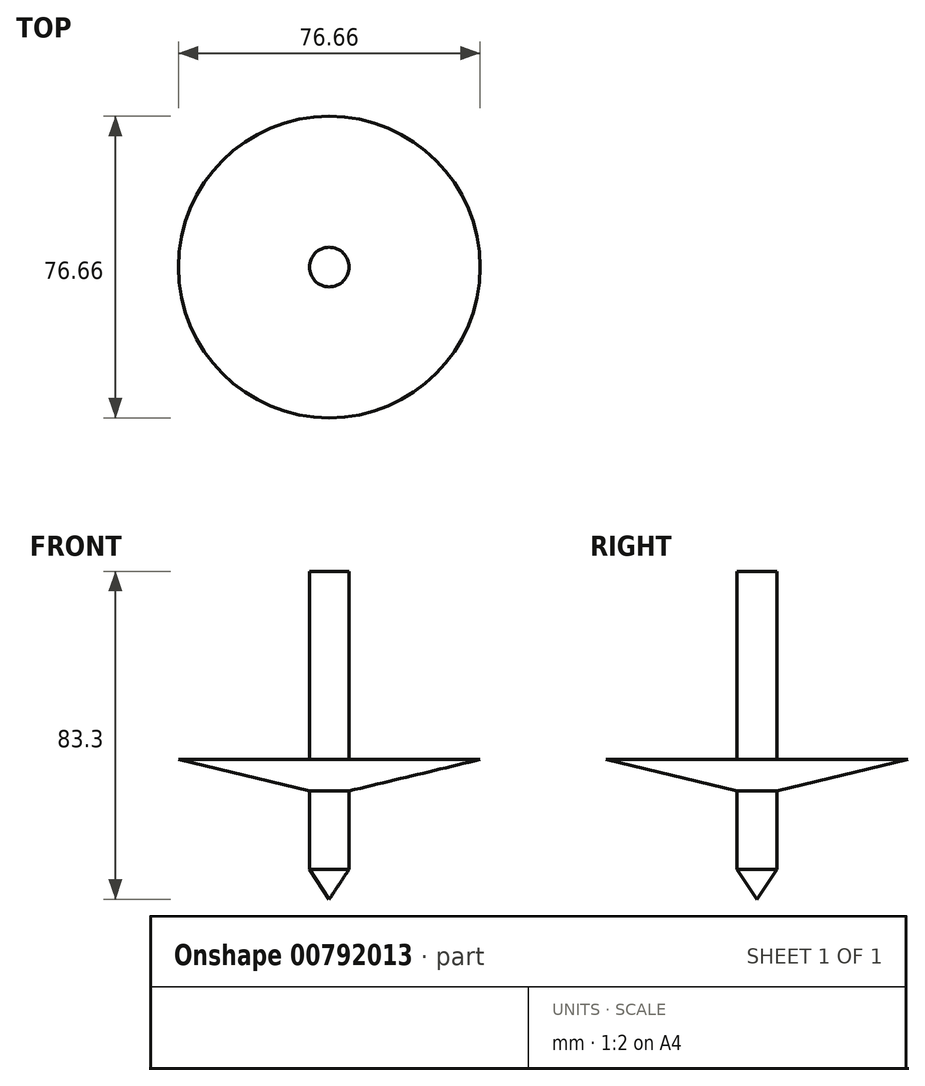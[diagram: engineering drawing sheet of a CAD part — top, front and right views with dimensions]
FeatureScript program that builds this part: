
annotation { "Feature Type Name" : "Feature", "Feature Type Description" : "" }
export const myFeature = defineFeature(function(context is Context, id is Id, definition is map)
    precondition{}
    {
        {
            var Q0;
            Q0=qCreatedBy(makeId("Front.planeOp"),FACE);
            var sketch = newSketch(context, id + "F0", { "sketchPlane" : qUnion([Q0])});
            skLineSegment(sketch, "E0", {"start": v(0, 47.79) * mm, "end": v(5.03, 47.79) * mm});
            skLineSegment(sketch, "E1", {"start": v(5.03, 47.79) * mm, "end": v(5.03, 0) * mm});
            skLineSegment(sketch, "E2", {"start": v(5.03, 0) * mm, "end": v(38.33, 0) * mm});
            skLineSegment(sketch, "E3", {"start": v(38.33, 0) * mm, "end": v(5.03, -7.98) * mm});
            skLineSegment(sketch, "E4", {"start": v(5.03, -7.98) * mm, "end": v(5.03, -27.89) * mm});
            skLineSegment(sketch, "E5", {"start": v(5.03, -27.89) * mm, "end": v(0, -35.5) * mm});
            skLineSegment(sketch, "E6", {"start": v(0, -35.5) * mm, "end": v(0, 47.79) * mm});
            skLineSegment(sketch, "E7", {"start": v(0, 47.79) * mm, "end": v(0, -35.5) * mm});
            skSolve(sketch);
        }
        {
            var Q0;
            Q0=makeQuery(id+"F0.imprint","IMPRINT",FACE,{"disambiguationData":[TD([[makeQuery(id+"F0.imprint","IMPRINT",EDGE,{"derivedFrom":sQuery(id+"F0.wireOp",EDGE,"E0")}),-1.0]])]});
            var Q1;
            Q1=sQuery(id+"F0.wireOp",EDGE,"E7");
            revolve(context, id + "F1", {"surfaceOperationType" : NewSurfaceOperationType.NEW, "entities" : qUnion([Q0]), "axis" : qUnion([Q1]), "revolveType" : RevolveType.FULL});
        }
    });
